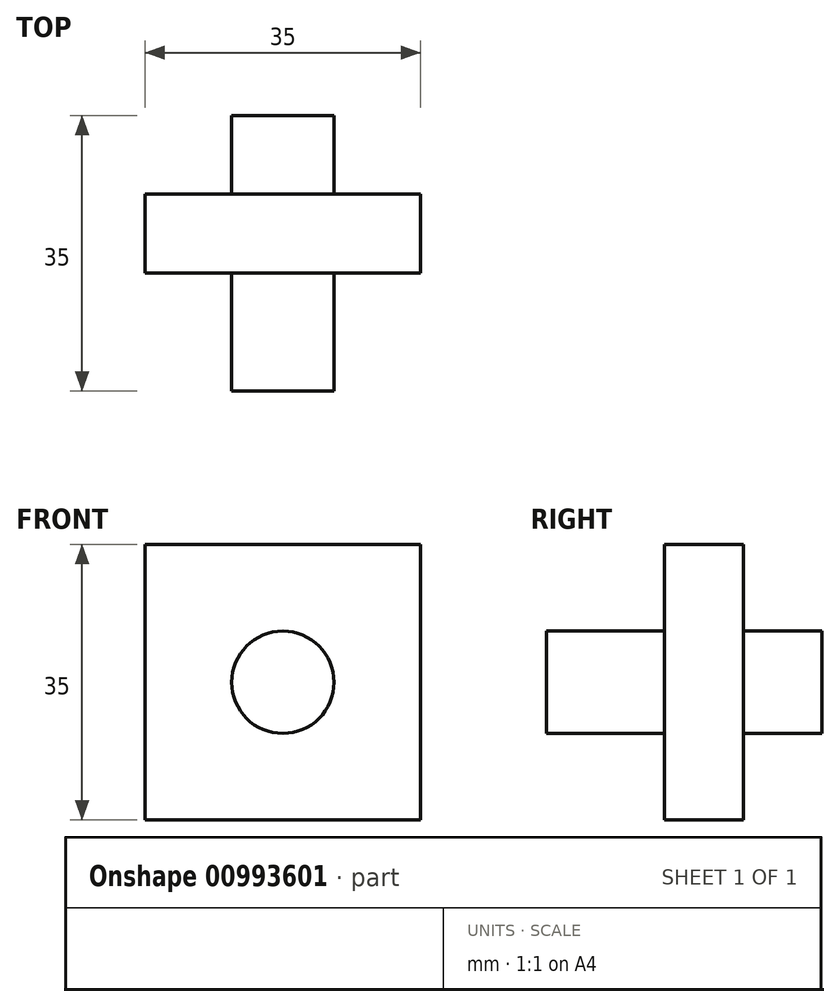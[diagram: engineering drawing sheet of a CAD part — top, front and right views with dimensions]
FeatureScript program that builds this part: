
annotation { "Feature Type Name" : "Feature", "Feature Type Description" : "" }
export const myFeature = defineFeature(function(context is Context, id is Id, definition is map)
    precondition{}
    {
        {
            var Q0;
            Q0=qCreatedBy(makeId("Front.planeOp"),FACE);
            var sketch = newSketch(context, id + "F0", { "sketchPlane" : qUnion([Q0])});
            skLineSegment(sketch, "E0.bottom", {"start": v(0, 0) * mm, "end": v(-35, 0) * mm});
            skLineSegment(sketch, "E0.top", {"start": v(0, 35) * mm, "end": v(-35, 35) * mm});
            skLineSegment(sketch, "E0.left", {"start": v(0, 0) * mm, "end": v(0, 35) * mm});
            skLineSegment(sketch, "E0.right", {"start": v(-35, 0) * mm, "end": v(-35, 35) * mm});
            skCircle(sketch, "E1", {"center": v(-17.5, 17.5) * mm, "radius": 6.5 * mm});
            skPoint(sketch, "E1.centerSnap0", {"position": v(-35, 17.5) * mm});
            skPoint(sketch, "E1.centerSnap1", {"position": v(-17.5, 35) * mm});
            skSolve(sketch);
        }
        {
            var Q0;
            Q0=qCreatedBy(makeId("Top.planeOp"),FACE);
            var sketch = newSketch(context, id + "F1", { "sketchPlane" : qUnion([Q0])});
            skLineSegment(sketch, "E2.bottom", {"start": v(0, 0) * mm, "end": v(-35, 0) * mm});
            skLineSegment(sketch, "E2.top", {"start": v(0, 20) * mm, "end": v(-35, 20) * mm});
            skLineSegment(sketch, "E2.left", {"start": v(0, 0) * mm, "end": v(0, 20) * mm});
            skLineSegment(sketch, "E2.right", {"start": v(-35, 0) * mm, "end": v(-35, 20) * mm});
            skSolve(sketch);
        }
        {
            var Q0;
            Q0 = qSketchRegion(id + "F1", true);
            extrude(context, id + "F2", {"entities" : qUnion([Q0]), "depth" : 30 * mm, "offsetDistance" : 25 * mm});
        }
        {
            var Q0;
            Q0=makeQuery(id+"F2.opExtrude","CAP_FACE",FACE,{"disambiguationData":[OSD([sQuery(id+"F1.wireOp",EDGE,"E2.bottom"),sQuery(id+"F1.wireOp",EDGE,"E2.top"),sQuery(id+"F1.wireOp",EDGE,"E2.left"),sQuery(id+"F1.wireOp",EDGE,"E2.right")])],"isStart":false});
            extrude(context, id + "F3", {"entities" : qUnion([Q0]), "operationType" : NewBodyOperationType.ADD, "depth" : 5 * mm, "offsetDistance" : 25 * mm});
        }
        {
            var Q0;
            Q0=makeQuery(id+"F0.imprint","IMPRINT",FACE,{"disambiguationData":[TD([[makeQuery(id+"F0.imprint","IMPRINT",EDGE,{"derivedFrom":sQuery(id+"F0.wireOp",EDGE,"E0.bottom")}),-1.0]])]});
            cPlane(context, id + "F4", {"entities" : qUnion([Q0]), "cplaneType" : CPlaneType.OFFSET, "offset" : 25 * mm, "width" : 150 * mm, "height" : 150 * mm});
        }
        {
            var Q0;
            Q0=qCreatedBy(id+"F4.planeOp",FACE);
            var sketch = newSketch(context, id + "F5", { "sketchPlane" : qUnion([Q0])});
            skSolve(sketch);
        }
        {
            var Q0;
            Q0 = qSketchRegion(id + "F5", true);
            var Q1;
            Q1=makeQuery(id+"F0.imprint","IMPRINT",FACE,{"disambiguationData":[TD([[makeQuery(id+"F0.imprint","IMPRINT",EDGE,{"derivedFrom":sQuery(id+"F0.wireOp",EDGE,"E1")}),1.0]])]});
            extrude(context, id + "F6", {"entities" : qUnion([Q0, Q1]), "operationType" : NewBodyOperationType.ADD, "depth" : 15 * mm, "offsetDistance" : 25 * mm});
        }
        {
            var Q0;
            {var subQ0=sQuery(id+"F1.wireOp",EDGE,"E2.bottom");Q0=makeQuery(id+"F3.boolean.opBoolean","MERGE",FACE,{"derivedFrom":[makeQuery(id+"F2.opExtrude","SWEPT_FACE",FACE,{"disambiguationData":[OSD([subQ0])]}),makeQuery(id+"F3.opExtrude","SWEPT_FACE",FACE,{"disambiguationData":[OSD([subQ0])]})]});}
            extrude(context, id + "F7", {"entities" : qUnion([Q0]), "operationType" : NewBodyOperationType.ADD, "oppositeDirection" : true, "depth" : 25 * mm, "offsetDistance" : 25 * mm});
        }
        {
            var Q0;
            Q0=makeQuery(id+"F7.opExtrude","CAP_FACE",FACE,{"disambiguationData":[OSD([sQuery(id+"F1.wireOp",EDGE,"E2.bottom")])],"isStart":false});
            extrude(context, id + "F8", {"entities" : qUnion([Q0]), "operationType" : NewBodyOperationType.ADD, "oppositeDirection" : true, "depth" : 15 * mm, "offsetDistance" : 25 * mm});
        }
        {
            var Q0;
            Q0=makeQuery(id+"F7.opExtrude","CAP_FACE",FACE,{"disambiguationData":[OSD([sQuery(id+"F1.wireOp",EDGE,"E2.bottom")])],"isStart":false});
            extrude(context, id + "F9", {"entities" : qUnion([Q0]), "operationType" : NewBodyOperationType.REMOVE, "oppositeDirection" : true, "depth" : 15 * mm, "offsetDistance" : 25 * mm});
        }
    });
